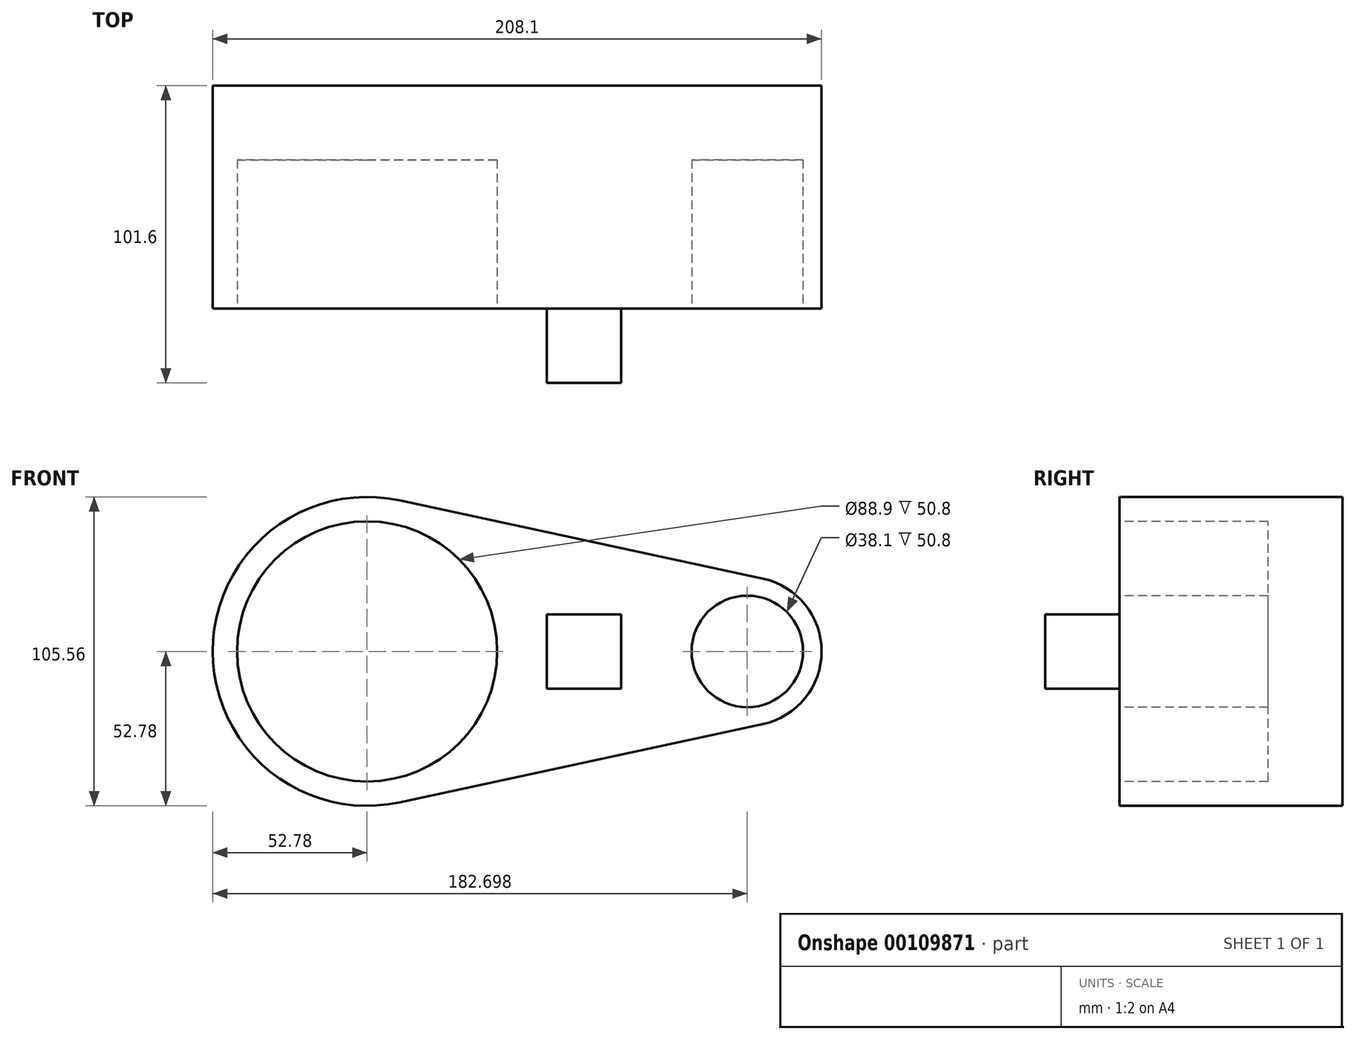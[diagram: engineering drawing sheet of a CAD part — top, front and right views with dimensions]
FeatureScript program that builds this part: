
annotation { "Feature Type Name" : "Feature", "Feature Type Description" : "" }
export const myFeature = defineFeature(function(context is Context, id is Id, definition is map)
    precondition{}
    {
        {
            var Q0;
            Q0=qCreatedBy(makeId("Front.planeOp"),FACE);
            var sketch = newSketch(context, id + "F0", { "sketchPlane" : qUnion([Q0])});
            skCircle(sketch, "E0", {"center": v(-60.43, 0) * mm, "radius": 52.78 * mm});
            skCircle(sketch, "E1", {"center": v(69.49, 0) * mm, "radius": 25.4 * mm});
            skLineSegment(sketch, "E2", {"start": v(-49.3, 51.6) * mm, "end": v(74.84, 24.83) * mm});
            skLineSegment(sketch, "E3", {"start": v(-49.3, -51.6) * mm, "end": v(74.84, -24.83) * mm});
            skSolve(sketch);
        }
        {
            var Q0;
            {var subQ0=sQuery(id+"F0.wireOp",EDGE,"E0");var subQ1=makeQuery(id+"F0.imprint","INTERSECT",VERTEX,{"derivedFrom":[subQ0,sQuery(id+"F0.wireOp",EDGE,"E2")]});Q0=makeQuery(id+"F0.imprint","IMPRINT",FACE,{"disambiguationData":[TD([[makeQuery(id+"F0.imprint","IMPRINT",EDGE,{"disambiguationData":[TD([[subQ1,-1.0]])],"derivedFrom":subQ0}),1.0]])]});}
            var Q1;
            {var subQ0=sQuery(id+"F0.wireOp",EDGE,"E2");Q1=makeQuery(id+"F0.imprint","IMPRINT",FACE,{"disambiguationData":[TD([[makeQuery(id+"F0.imprint","IMPRINT",EDGE,{"derivedFrom":subQ0}),-1.0]])]});}
            var Q2;
            {var subQ0=sQuery(id+"F0.wireOp",EDGE,"E1");var subQ1=makeQuery(id+"F0.imprint","INTERSECT",VERTEX,{"derivedFrom":[subQ0,sQuery(id+"F0.wireOp",EDGE,"E2")]});Q2=makeQuery(id+"F0.imprint","IMPRINT",FACE,{"disambiguationData":[TD([[makeQuery(id+"F0.imprint","IMPRINT",EDGE,{"disambiguationData":[TD([[subQ1,-1.0]])],"derivedFrom":subQ0}),1.0]])]});}
            extrude(context, id + "F1", {"entities" : qUnion([Q0, Q1, Q2]), "depth" : 76.2 * mm});
        }
        {
            var Q0;
            Q0=makeQuery(id+"F1.opExtrude","CAP_FACE",FACE,{"disambiguationData":[OSD([sQuery(id+"F0.wireOp",EDGE,"E0"),sQuery(id+"F0.wireOp",EDGE,"E1"),sQuery(id+"F0.wireOp",EDGE,"E2"),sQuery(id+"F0.wireOp",EDGE,"E3")])],"isStart":false});
            var sketch = newSketch(context, id + "F2", { "sketchPlane" : qUnion([Q0])});
            skCircle(sketch, "E4", {"center": v(-60.43, 0) * mm, "radius": 44.45 * mm});
            skSolve(sketch);
        }
        {
            var Q0;
            Q0=makeQuery(id+"F2.imprint","IMPRINT",FACE,{"disambiguationData":[TD([[makeQuery(id+"F2.imprint","IMPRINT",EDGE,{"derivedFrom":sQuery(id+"F2.wireOp",EDGE,"E4")}),1.0]])]});
            extrude(context, id + "F3", {"entities" : qUnion([Q0]), "operationType" : NewBodyOperationType.REMOVE, "oppositeDirection" : true, "depth" : 50.8 * mm});
        }
        {
            var Q0;
            Q0=makeQuery(id+"F1.opExtrude","CAP_FACE",FACE,{"disambiguationData":[OSD([sQuery(id+"F0.wireOp",EDGE,"E0"),sQuery(id+"F0.wireOp",EDGE,"E1"),sQuery(id+"F0.wireOp",EDGE,"E2"),sQuery(id+"F0.wireOp",EDGE,"E3")])],"isStart":false});
            var sketch = newSketch(context, id + "F4", { "sketchPlane" : qUnion([Q0])});
            skCircle(sketch, "E5", {"center": v(69.49, 0) * mm, "radius": 19.05 * mm});
            skSolve(sketch);
        }
        {
            var Q0;
            Q0=makeQuery(id+"F4.imprint","IMPRINT",FACE,{"disambiguationData":[TD([[makeQuery(id+"F4.imprint","IMPRINT",EDGE,{"derivedFrom":sQuery(id+"F4.wireOp",EDGE,"E5")}),1.0]])]});
            extrude(context, id + "F5", {"entities" : qUnion([Q0]), "operationType" : NewBodyOperationType.REMOVE, "oppositeDirection" : true, "depth" : 50.8 * mm});
        }
        {
            var Q0;
            Q0=makeQuery(id+"F1.opExtrude","CAP_FACE",FACE,{"disambiguationData":[OSD([sQuery(id+"F0.wireOp",EDGE,"E0"),sQuery(id+"F0.wireOp",EDGE,"E1"),sQuery(id+"F0.wireOp",EDGE,"E2"),sQuery(id+"F0.wireOp",EDGE,"E3")])],"isStart":false});
            var sketch = newSketch(context, id + "F6", { "sketchPlane" : qUnion([Q0])});
            skLineSegment(sketch, "E6.bottom", {"start": v(0.98, 12.7) * mm, "end": v(26.38, 12.7) * mm});
            skLineSegment(sketch, "E6.top", {"start": v(0.98, -12.7) * mm, "end": v(26.38, -12.7) * mm});
            skLineSegment(sketch, "E6.left", {"start": v(0.98, 12.7) * mm, "end": v(0.98, -12.7) * mm});
            skLineSegment(sketch, "E6.right", {"start": v(26.38, 12.7) * mm, "end": v(26.38, -12.7) * mm});
            skSolve(sketch);
        }
        {
            var Q0;
            Q0=makeQuery(id+"F6.imprint","IMPRINT",FACE,{"disambiguationData":[TD([[makeQuery(id+"F6.imprint","IMPRINT",EDGE,{"derivedFrom":sQuery(id+"F6.wireOp",EDGE,"E6.bottom")}),-1.0]])]});
            extrude(context, id + "F7", {"entities" : qUnion([Q0]), "operationType" : NewBodyOperationType.ADD, "depth" : 25.4 * mm});
        }
    });
